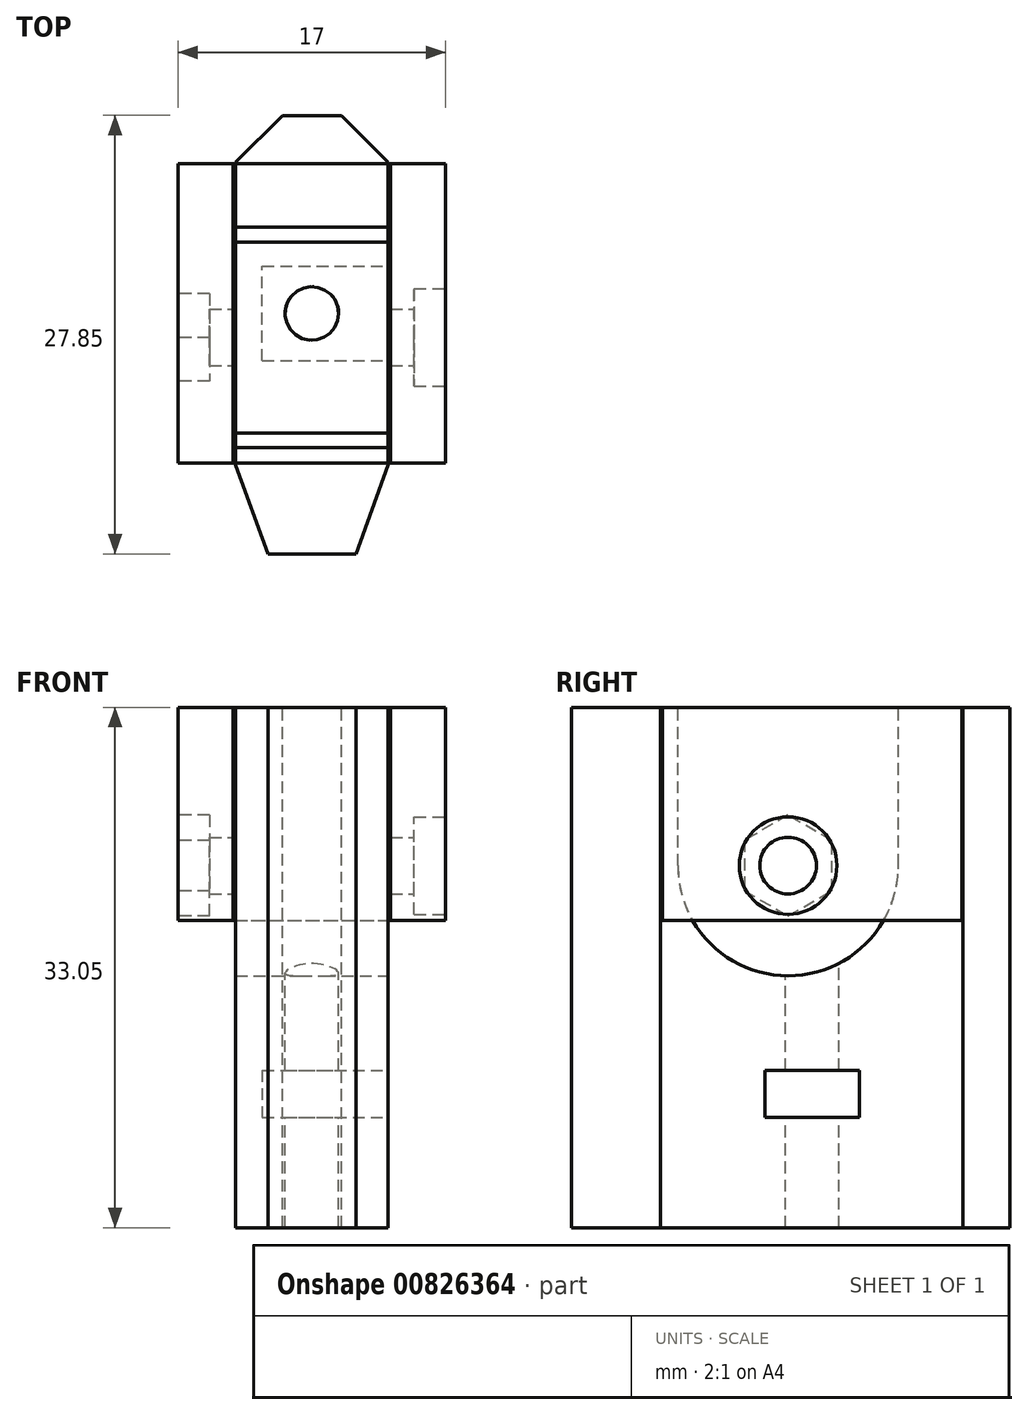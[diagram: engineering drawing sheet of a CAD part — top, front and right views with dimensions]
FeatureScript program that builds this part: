
annotation { "Feature Type Name" : "Feature", "Feature Type Description" : "" }
export const myFeature = defineFeature(function(context is Context, id is Id, definition is map)
    precondition{}
    {
        {
            var Q0;
            Q0=qCreatedBy(makeId("Top.planeOp"),FACE);
            var sketch = newSketch(context, id + "F0", { "sketchPlane" : qUnion([Q0])});
            skLineSegment(sketch, "E0", {"start": v(-25.67, 0) * mm, "end": v(37.09, 0) * mm, "construction": true});
            skLineSegment(sketch, "E1", {"start": v(0, 12.73) * mm, "end": v(-1.93, 12.73) * mm, "construction": true});
            skLineSegment(sketch, "E2", {"start": v(-1.93, 12.73) * mm, "end": v(-5, 9.66) * mm, "construction": true});
            skLineSegment(sketch, "E3", {"start": v(-5, -9.66) * mm, "end": v(-2.95, -15.27) * mm, "construction": true});
            skLineSegment(sketch, "E4", {"start": v(-2.96, -15.27) * mm, "end": v(0, -15.27) * mm, "construction": true});
            skLineSegment(sketch, "E5", {"start": v(0, -31.85) * mm, "end": v(0, 31.57) * mm, "construction": true});
            skLineSegment(sketch, "E6.1", {"start": v(-4.85, -9.63) * mm, "end": v(-2.85, -15.12) * mm});
            skLineSegment(sketch, "E6.2", {"start": v(0, 12.58) * mm, "end": v(-1.87, 12.58) * mm});
            skLineSegment(sketch, "E6.3", {"start": v(-1.87, 12.58) * mm, "end": v(-4.85, 9.6) * mm});
            skLineSegment(sketch, "E6.4", {"start": v(-4.85, 9.6) * mm, "end": v(-4.85, 0) * mm});
            skLineSegment(sketch, "E6.5", {"start": v(-4.85, 0) * mm, "end": v(-4.85, -9.63) * mm});
            skLineSegment(sketch, "E7.MirrorCS", {"start": v(0, 12.58) * mm, "end": v(1.87, 12.58) * mm});
            skLineSegment(sketch, "E8.MirrorCS", {"start": v(1.87, 12.58) * mm, "end": v(4.85, 9.6) * mm});
            skLineSegment(sketch, "E9.MirrorCS", {"start": v(4.85, 9.6) * mm, "end": v(4.85, 0) * mm});
            skLineSegment(sketch, "E10.MirrorCS", {"start": v(4.85, 0) * mm, "end": v(4.85, -9.63) * mm});
            skLineSegment(sketch, "E11.MirrorCS", {"start": v(4.85, -9.63) * mm, "end": v(2.85, -15.12) * mm});
            skCircle(sketch, "E12", {"center": v(0, 0) * mm, "radius": 1.7 * mm});
            skLineSegment(sketch, "E13", {"start": v(-5, 9.5) * mm, "end": v(-8.5, 9.5) * mm});
            skLineSegment(sketch, "E14", {"start": v(-8.5, 9.5) * mm, "end": v(-8.5, 0) * mm});
            skLineSegment(sketch, "E15", {"start": v(-5, 9.5) * mm, "end": v(-5, 0) * mm});
            skLineSegment(sketch, "E16.MirrorCS", {"start": v(-8.5, -9.5) * mm, "end": v(-8.5, 0) * mm});
            skLineSegment(sketch, "E17.MirrorCS", {"start": v(-5, -9.5) * mm, "end": v(-8.5, -9.5) * mm});
            skLineSegment(sketch, "E18.MirrorCS", {"start": v(-5, -9.5) * mm, "end": v(-5, 0) * mm});
            skLineSegment(sketch, "E19.MirrorCS", {"start": v(5, 9.5) * mm, "end": v(8.5, 9.5) * mm});
            skLineSegment(sketch, "E20.MirrorCS", {"start": v(8.5, 9.5) * mm, "end": v(8.5, 0) * mm});
            skLineSegment(sketch, "E21.MirrorCS", {"start": v(8.5, -9.5) * mm, "end": v(8.5, 0) * mm});
            skLineSegment(sketch, "E22.MirrorCS", {"start": v(5, -9.5) * mm, "end": v(8.5, -9.5) * mm});
            skLineSegment(sketch, "E23.MirrorCS", {"start": v(5, -9.5) * mm, "end": v(5, 0) * mm});
            skLineSegment(sketch, "E24.MirrorCS", {"start": v(5, 9.5) * mm, "end": v(5, 0) * mm});
            skPoint(sketch, "E25", {"position": v(0, 12.73) * mm});
            skLineSegment(sketch, "E26", {"start": v(-2.85, -15.12) * mm, "end": v(-2.8, -15.27) * mm});
            skLineSegment(sketch, "E27.MirrorCS", {"start": v(2.85, -15.12) * mm, "end": v(2.8, -15.27) * mm});
            skLineSegment(sketch, "E28", {"start": v(-2.8, -15.27) * mm, "end": v(2.8, -15.27) * mm});
            skSolve(sketch);
        }
        {
            var Q0;
            Q0=makeQuery(id+"F0.imprint","IMPRINT",FACE,{"disambiguationData":[TD([[makeQuery(id+"F0.imprint","IMPRINT",EDGE,{"derivedFrom":sQuery(id+"F0.wireOp",EDGE,"E13")}),1.0]])]});
            var Q1;
            Q1=makeQuery(id+"F0.imprint","IMPRINT",FACE,{"disambiguationData":[TD([[makeQuery(id+"F0.imprint","IMPRINT",EDGE,{"derivedFrom":sQuery(id+"F0.wireOp",EDGE,"E19.MirrorCS")}),-1.0]])]});
            extrude(context, id + "F1", {"entities" : qUnion([Q0, Q1]), "depth" : 18.05 * mm, "offsetDistance" : 25 * mm});
        }
        {
            var Q0;
            Q0=makeQuery(id+"F1.opExtrude","SWEPT_FACE",FACE,{"disambiguationData":[OSD([sQuery(id+"F0.wireOp",EDGE,"E20.MirrorCS"),sQuery(id+"F0.wireOp",EDGE,"E21.MirrorCS")])]});
            var sketch = newSketch(context, id + "F2", { "sketchPlane" : qUnion([Q0])});
            skLineSegment(sketch, "E29.bottom", {"start": v(9.5, 0) * mm, "end": v(-9.5, 0) * mm});
            skLineSegment(sketch, "E29.top", {"start": v(9.5, 4.5) * mm, "end": v(-9.5, 4.5) * mm});
            skLineSegment(sketch, "E29.left", {"start": v(9.5, 0) * mm, "end": v(9.5, 4.5) * mm});
            skLineSegment(sketch, "E29.right", {"start": v(-9.5, 0) * mm, "end": v(-9.5, 4.5) * mm});
            skSolve(sketch);
        }
        {
            var Q0;
            Q0=makeQuery(id+"F2.imprint","IMPRINT",FACE,{"disambiguationData":[TD([[makeQuery(id+"F2.imprint","IMPRINT",EDGE,{"derivedFrom":sQuery(id+"F2.wireOp",EDGE,"E29.bottom")}),1.0]])]});
            extrude(context, id + "F3", {"entities" : qUnion([Q0]), "operationType" : NewBodyOperationType.REMOVE, "endBound" : BoundingType.THROUGH_ALL, "oppositeDirection" : true, "depth" : 3.5 * mm, "offsetDistance" : 25 * mm});
        }
        {
            var Q0;
            Q0=makeQuery(id+"F0.imprint","IMPRINT",FACE,{"disambiguationData":[TD([[makeQuery(id+"F0.imprint","IMPRINT",EDGE,{"derivedFrom":sQuery(id+"F0.wireOp",EDGE,"E6.1")}),1.0]])]});
            extrude(context, id + "F4", {"entities" : qUnion([Q0]), "oppositeDirection" : true, "depth" : 15 * mm, "offsetDistance" : 25 * mm, "hasSecondDirection" : true, "secondDirectionOppositeDirection" : false, "secondDirectionDepth" : 18.05 * mm});
        }
        {
            var Q0;
            Q0=makeQuery(id+"F1.opExtrude","SWEPT_FACE",FACE,{"disambiguationData":[OSD([sQuery(id+"F0.wireOp",EDGE,"E20.MirrorCS"),sQuery(id+"F0.wireOp",EDGE,"E21.MirrorCS")])]});
            var sketch = newSketch(context, id + "F5", { "sketchPlane" : qUnion([Q0])});
            skLineSegment(sketch, "E30", {"start": v(-1.52, 43.26) * mm, "end": v(-1.52, -42.48) * mm, "construction": true});
            skLineSegment(sketch, "E31", {"start": v(28.04, 8) * mm, "end": v(-29.93, 8) * mm, "construction": true});
            skPoint(sketch, "E32", {"position": v(-1.52, 8) * mm});
            skCircle(sketch, "E33", {"center": v(-1.52, 8) * mm, "radius": 6.5 * mm, "construction": true});
            skSolve(sketch);
        }
        {
            var Q0;
            Q0=sQuery(id+"F5.wireOp",VERTEX,"E32");
            var Q1;
            Q1=makeQuery(id+"F1.opExtrude","SWEPT_BODY",BODY,{"disambiguationData":[OSD([sQuery(id+"F0.wireOp",EDGE,"E19.MirrorCS"),sQuery(id+"F0.wireOp",EDGE,"E20.MirrorCS"),sQuery(id+"F0.wireOp",EDGE,"E21.MirrorCS"),sQuery(id+"F0.wireOp",EDGE,"E22.MirrorCS"),sQuery(id+"F0.wireOp",EDGE,"E23.MirrorCS"),sQuery(id+"F0.wireOp",EDGE,"E24.MirrorCS")])]});
            var Q2;
            Q2=makeQuery(id+"F1.opExtrude","SWEPT_BODY",BODY,{"disambiguationData":[OSD([sQuery(id+"F0.wireOp",EDGE,"E13"),sQuery(id+"F0.wireOp",EDGE,"E14"),sQuery(id+"F0.wireOp",EDGE,"E15"),sQuery(id+"F0.wireOp",EDGE,"E16.MirrorCS"),sQuery(id+"F0.wireOp",EDGE,"E17.MirrorCS"),sQuery(id+"F0.wireOp",EDGE,"E18.MirrorCS")])]});
            hole(context, id + "F6", {"style" : HoleStyle.C_BORE, "endStyle" : HoleEndStyle.THROUGH, "holeDiameter" : 3.6 * mm, "cBoreDiameter" : 6.2 * mm, "cBoreDepth" : 2 * mm, "majorDiameter" : 5 * mm, "isTappedThrough" : true, "tappedDepth" : 12 * mm, "tapClearance" : 3, "startFromSketch" : true, "locations" : qUnion([Q0]), "scope" : qUnion([Q1, Q2])});
        }
        {
            var Q0;
            Q0=makeQuery(id+"F1.opExtrude","SWEPT_FACE",FACE,{"disambiguationData":[OSD([sQuery(id+"F0.wireOp",EDGE,"E14"),sQuery(id+"F0.wireOp",EDGE,"E16.MirrorCS")])]});
            var sketch = newSketch(context, id + "F7", { "sketchPlane" : qUnion([Q0])});
            skCircle(sketch, "E34.cCircle", {"center": v(1.52, 8) * mm, "radius": 2.77 * mm, "construction": true});
            skLineSegment(sketch, "E34.0", {"start": v(4.3, 9.6) * mm, "end": v(4.3, 6.4) * mm});
            skLineSegment(sketch, "E34.1", {"start": v(4.3, 6.4) * mm, "end": v(1.52, 4.8) * mm});
            skLineSegment(sketch, "E34.2", {"start": v(1.52, 4.8) * mm, "end": v(-1.25, 6.4) * mm});
            skLineSegment(sketch, "E34.3", {"start": v(-1.25, 6.4) * mm, "end": v(-1.25, 9.6) * mm});
            skLineSegment(sketch, "E34.4", {"start": v(-1.25, 9.6) * mm, "end": v(1.52, 11.2) * mm});
            skLineSegment(sketch, "E34.5", {"start": v(1.52, 11.2) * mm, "end": v(4.3, 9.6) * mm});
            skPoint(sketch, "E34.0.midPoint", {"position": v(4.3, 8) * mm});
            skSolve(sketch);
        }
        {
            var Q0;
            Q0=makeQuery(id+"F7.imprint","IMPRINT",FACE,{"disambiguationData":[TD([[makeQuery(id+"F7.imprint","IMPRINT",EDGE,{"derivedFrom":sQuery(id+"F7.wireOp",EDGE,"E34.0")}),-1.0]])]});
            extrude(context, id + "F8", {"entities" : qUnion([Q0]), "operationType" : NewBodyOperationType.REMOVE, "oppositeDirection" : true, "depth" : 2 * mm, "offsetDistance" : 25 * mm});
        }
        {
            var Q0;
            Q0=makeQuery(id+"F4.opExtrude","SWEPT_FACE",FACE,{"disambiguationData":[OSD([sQuery(id+"F0.wireOp",EDGE,"E9.MirrorCS"),sQuery(id+"F0.wireOp",EDGE,"E10.MirrorCS")])]});
            var sketch = newSketch(context, id + "F9", { "sketchPlane" : qUnion([Q0])});
            skLineSegment(sketch, "E35", {"start": v(0, -5) * mm, "end": v(3, -5) * mm});
            skLineSegment(sketch, "E36", {"start": v(3, -5) * mm, "end": v(3, -8) * mm});
            skLineSegment(sketch, "E37", {"start": v(3, -8) * mm, "end": v(0, -8) * mm});
            skLineSegment(sketch, "E38.MirrorCS", {"start": v(0, -5) * mm, "end": v(-3, -5) * mm});
            skLineSegment(sketch, "E39.MirrorCS", {"start": v(-3, -5) * mm, "end": v(-3, -8) * mm});
            skLineSegment(sketch, "E40.MirrorCS", {"start": v(-3, -8) * mm, "end": v(0, -8) * mm});
            skArc(sketch, "E41", {"start": v(-8.52, 8) * mm, "mid": v(-1.52, 1) * mm, "end": v(5.48, 8) * mm});
            skLineSegment(sketch, "E42", {"start": v(5.48, 8) * mm, "end": v(5.48, 18.05) * mm});
            skLineSegment(sketch, "E43", {"start": v(-8.52, 8) * mm, "end": v(-8.52, 18.05) * mm});
            skLineSegment(sketch, "E44", {"start": v(5.48, 18.05) * mm, "end": v(-8.52, 18.05) * mm});
            skLineSegment(sketch, "E45", {"start": v(-7.59, 4.5) * mm, "end": v(-9.5, 4.5) * mm});
            skLineSegment(sketch, "E46", {"start": v(-9.5, 4.5) * mm, "end": v(-9.5, 18.05) * mm});
            skLineSegment(sketch, "E47", {"start": v(-9.5, 18.05) * mm, "end": v(-8.52, 18.05) * mm});
            skLineSegment(sketch, "E48", {"start": v(4.54, 4.5) * mm, "end": v(9.5, 4.5) * mm});
            skLineSegment(sketch, "E49", {"start": v(9.5, 4.5) * mm, "end": v(9.5, 18.05) * mm});
            skLineSegment(sketch, "E50", {"start": v(9.5, 18.05) * mm, "end": v(5.48, 18.05) * mm});
            skSolve(sketch);
        }
        {
            var Q0;
            Q0=makeQuery(id+"F9.imprint","IMPRINT",FACE,{"disambiguationData":[TD([[makeQuery(id+"F9.imprint","IMPRINT",EDGE,{"derivedFrom":sQuery(id+"F9.wireOp",EDGE,"E35")}),-1.0]])]});
            extrude(context, id + "F10", {"entities" : qUnion([Q0]), "operationType" : NewBodyOperationType.REMOVE, "oppositeDirection" : true, "depth" : 8 * mm, "offsetDistance" : 25 * mm});
        }
        {
            var Q0;
            Q0=makeQuery(id+"F9.imprint","IMPRINT",FACE,{"disambiguationData":[TD([[makeQuery(id+"F9.imprint","IMPRINT",EDGE,{"derivedFrom":sQuery(id+"F9.wireOp",EDGE,"E41")}),1.0]])]});
            var Q1;
            Q1=makeQuery(id+"F4.opExtrude","SWEPT_BODY",BODY,{"disambiguationData":[OSD([sQuery(id+"F0.wireOp",EDGE,"E6.0"),sQuery(id+"F0.wireOp",EDGE,"E6.1"),sQuery(id+"F0.wireOp",EDGE,"E6.2"),sQuery(id+"F0.wireOp",EDGE,"E6.3"),sQuery(id+"F0.wireOp",EDGE,"E6.4"),sQuery(id+"F0.wireOp",EDGE,"E6.5"),sQuery(id+"F0.wireOp",EDGE,"E7.MirrorCS"),sQuery(id+"F0.wireOp",EDGE,"E8.MirrorCS"),sQuery(id+"F0.wireOp",EDGE,"E9.MirrorCS"),sQuery(id+"F0.wireOp",EDGE,"E10.MirrorCS"),sQuery(id+"F0.wireOp",EDGE,"E11.MirrorCS"),sQuery(id+"F0.wireOp",EDGE,"37bbc0db-56eb-4107-8967-c16d97b151150.MirrorCS"),sQuery(id+"F0.wireOp",EDGE,"E12")])]});
            extrude(context, id + "F11", {"entities" : qUnion([Q0]), "operationType" : NewBodyOperationType.REMOVE, "endBound" : BoundingType.UP_TO_BODY, "oppositeDirection" : true, "depth" : 5 * mm, "endBoundEntityBody" : qUnion([Q1]), "offsetDistance" : 25 * mm});
        }
        {
            var Q0;
            {var subQ1=sQuery(id+"F9.wireOp",EDGE,"E43");Q0=makeQuery(id+"F9.imprint","IMPRINT",FACE,{"disambiguationData":[TD([[makeQuery(id+"F9.imprint","IMPRINT",EDGE,{"derivedFrom":subQ1}),1.0]])]});}
            var Q1;
            {var subQ1=sQuery(id+"F9.wireOp",EDGE,"E42");Q1=makeQuery(id+"F9.imprint","IMPRINT",FACE,{"disambiguationData":[TD([[makeQuery(id+"F9.imprint","IMPRINT",EDGE,{"derivedFrom":subQ1}),-1.0]])]});}
            var Q2;
            Q2=makeQuery(id+"F1.opExtrude","SWEPT_FACE",FACE,{"disambiguationData":[OSD([sQuery(id+"F0.wireOp",EDGE,"E15"),sQuery(id+"F0.wireOp",EDGE,"E18.MirrorCS")])]});
            var Q3;
            Q3=makeQuery(id+"F1.opExtrude","SWEPT_FACE",FACE,{"disambiguationData":[OSD([sQuery(id+"F0.wireOp",EDGE,"E23.MirrorCS"),sQuery(id+"F0.wireOp",EDGE,"E24.MirrorCS")])]});
            extrude(context, id + "F12", {"entities" : qUnion([Q0, Q1]), "endBound" : BoundingType.UP_TO_SURFACE, "oppositeDirection" : true, "depth" : 25 * mm, "endBoundEntityFace" : qUnion([Q2]), "offsetDistance" : 25 * mm, "hasSecondDirection" : true, "secondDirectionBound" : SecondDirectionBoundingType.UP_TO_SURFACE, "secondDirectionOppositeDirection" : false, "secondDirectionDepth" : 25 * mm, "secondDirectionBoundEntityFace" : qUnion([Q3])});
        }
    });
